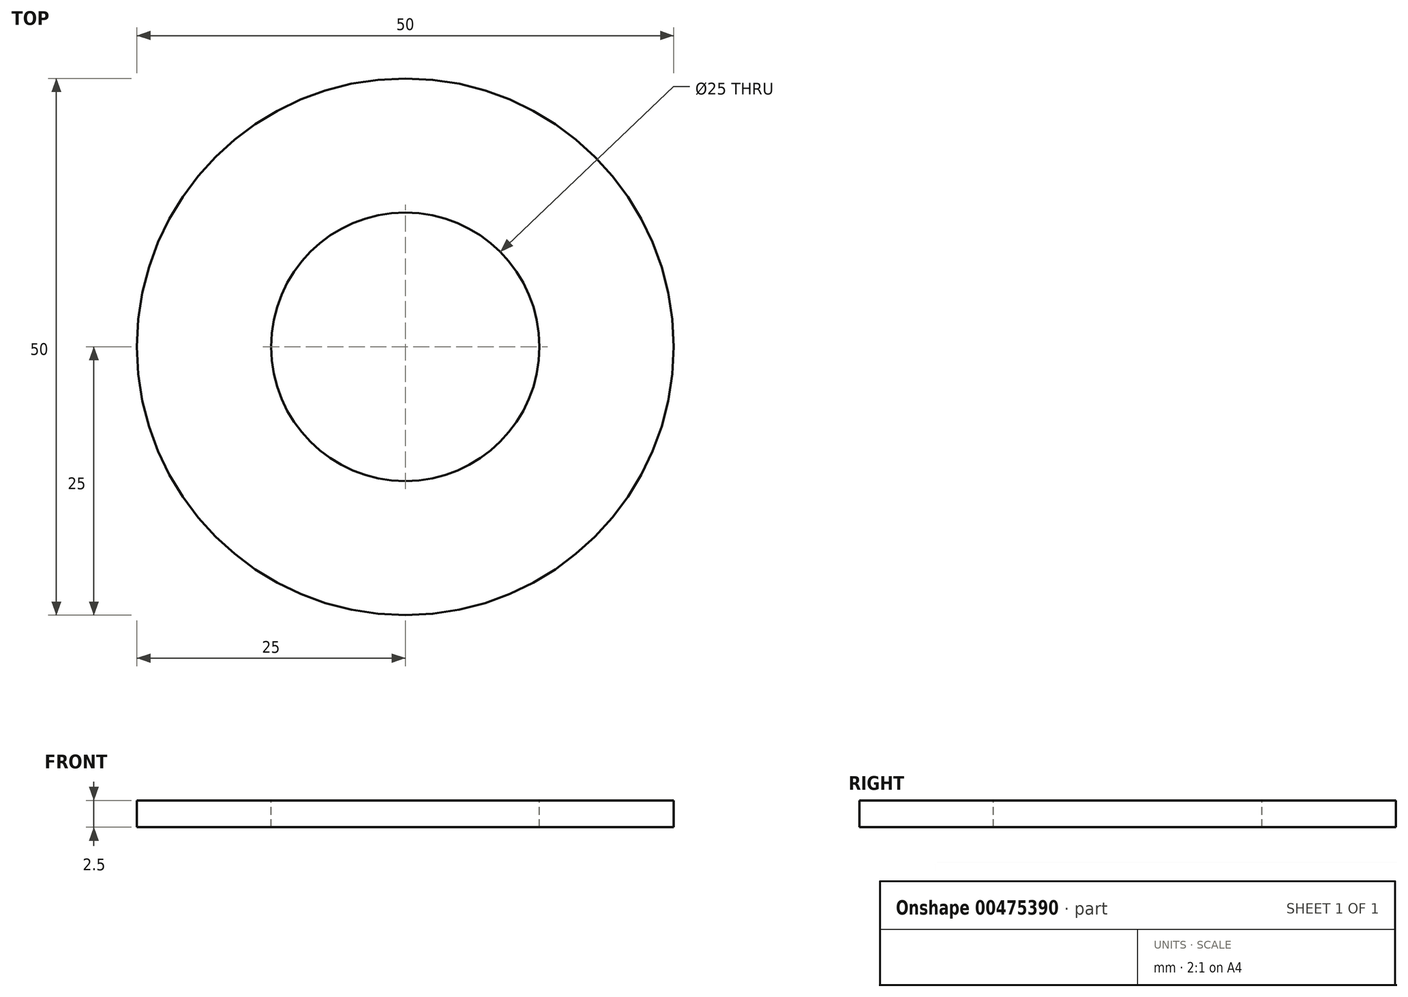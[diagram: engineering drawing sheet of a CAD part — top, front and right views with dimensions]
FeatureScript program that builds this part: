
annotation { "Feature Type Name" : "Feature", "Feature Type Description" : "" }
export const myFeature = defineFeature(function(context is Context, id is Id, definition is map)
    precondition{}
    {
        {
            var Q0;
            Q0=qCreatedBy(makeId("Top.planeOp"),FACE);
            var sketch = newSketch(context, id + "F0", { "sketchPlane" : qUnion([Q0])});
            skCircle(sketch, "E0", {"center": v(0, 0) * mm, "radius": 25 * mm});
            skCircle(sketch, "E1", {"center": v(0, 0) * mm, "radius": 12.5 * mm});
            skSolve(sketch);
        }
        {
            var Q0;
            Q0 = qSketchRegion(id + "F0", true);
            var Q1;
            Q1=makeQuery(id+"F0.imprint","IMPRINT",FACE,{"disambiguationData":[TD([[makeQuery(id+"F0.imprint","IMPRINT",EDGE,{"derivedFrom":sQuery(id+"F0.wireOp",EDGE,"E0")}),1.0]])]});
            extrude(context, id + "F1", {"entities" : qUnion([Q0, Q1]), "oppositeDirection" : true, "depth" : 2.5 * mm, "offsetDistance" : 25 * mm});
        }
    });
